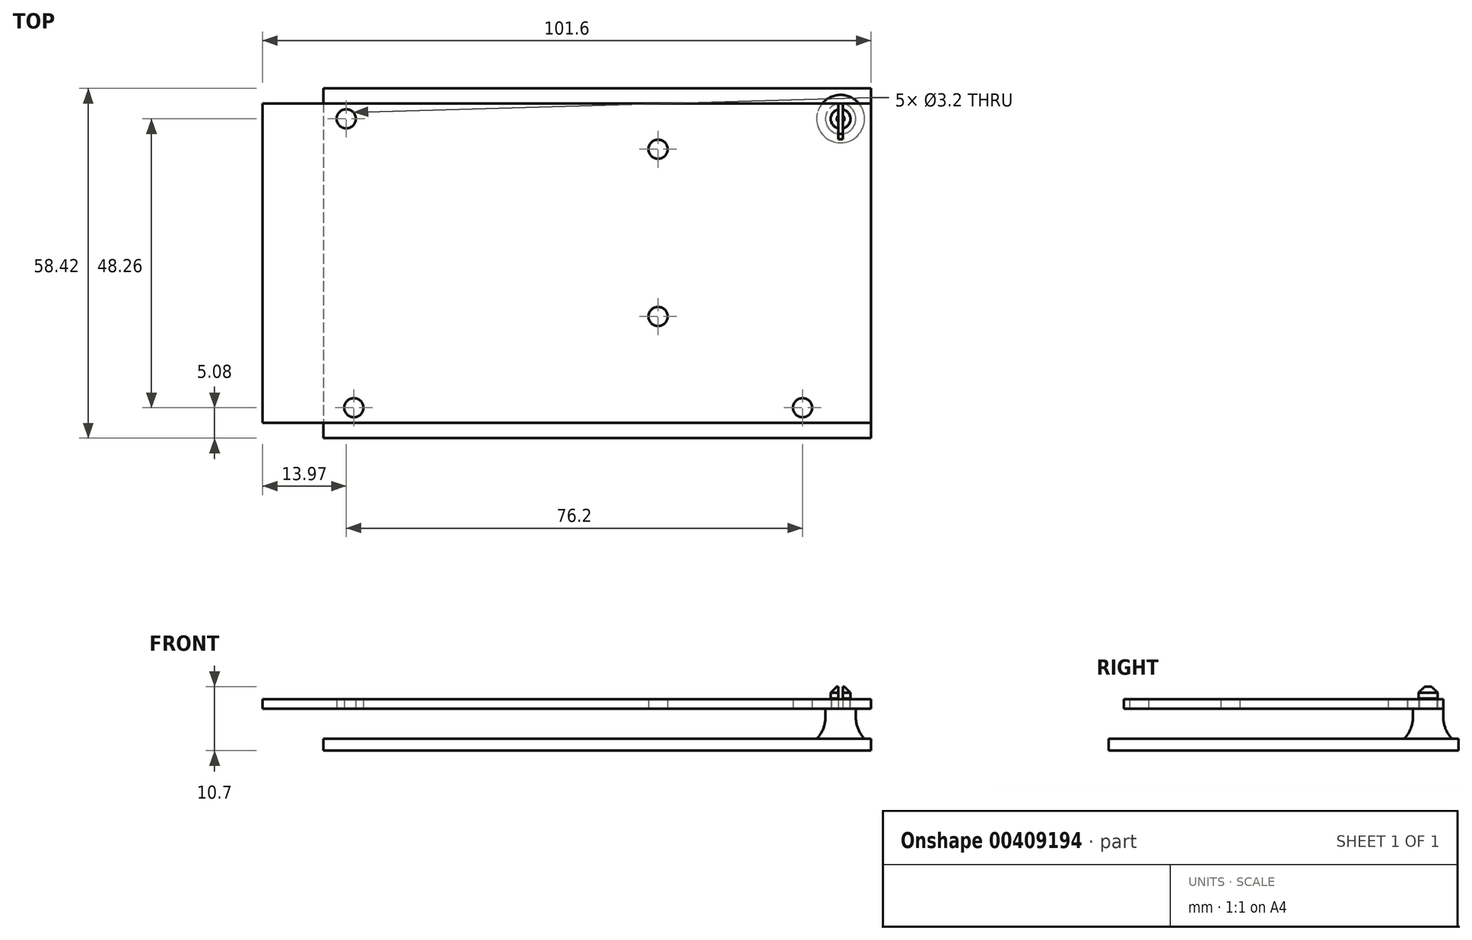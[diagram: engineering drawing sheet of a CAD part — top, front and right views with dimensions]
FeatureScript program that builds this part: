
annotation { "Feature Type Name" : "Feature", "Feature Type Description" : "" }
export const myFeature = defineFeature(function(context is Context, id is Id, definition is map)
    precondition{}
    {
        {
            var Q0;
            Q0=qCreatedBy(makeId("Top.planeOp"),FACE);
            var sketch = newSketch(context, id + "F0", { "sketchPlane" : qUnion([Q0])});
            skLineSegment(sketch, "E0.bottom", {"start": v(-50.8, -26.67) * mm, "end": v(50.8, -26.67) * mm});
            skLineSegment(sketch, "E0.top", {"start": v(-50.8, 26.67) * mm, "end": v(50.8, 26.67) * mm});
            skLineSegment(sketch, "E0.left", {"start": v(-50.8, -26.67) * mm, "end": v(-50.8, 26.67) * mm});
            skLineSegment(sketch, "E0.right", {"start": v(50.8, -26.67) * mm, "end": v(50.8, 26.67) * mm});
            skCircle(sketch, "E1", {"center": v(45.72, 24.13) * mm, "radius": 1.6 * mm});
            skCircle(sketch, "E2", {"center": v(15.24, 19.05) * mm, "radius": 1.6 * mm});
            skCircle(sketch, "E3", {"center": v(15.24, -8.9) * mm, "radius": 1.6 * mm});
            skCircle(sketch, "E4", {"center": v(39.37, -24.13) * mm, "radius": 1.6 * mm});
            skCircle(sketch, "E5", {"center": v(-35.56, -24.13) * mm, "radius": 1.6 * mm});
            skCircle(sketch, "E6", {"center": v(-36.83, 24.13) * mm, "radius": 1.6 * mm});
            skLineSegment(sketch, "E7", {"start": v(-36.83, 24.13) * mm, "end": v(45.72, 24.13) * mm, "construction": true});
            skLineSegment(sketch, "E8", {"start": v(-35.56, -24.13) * mm, "end": v(39.37, -24.13) * mm, "construction": true});
            skLineSegment(sketch, "E9", {"start": v(15.24, 19.05) * mm, "end": v(15.24, -8.9) * mm, "construction": true});
            skSolve(sketch);
        }
        {
            var Q0;
            Q0 = qSketchRegion(id + "F0", true);
            extrude(context, id + "F1", {"entities" : qUnion([Q0]), "depth" : 1.6 * mm});
        }
        {
            var Q0;
            Q0=makeQuery(id+"F1.opExtrude","CAP_FACE",FACE,{"disambiguationData":[OSD([sQuery(id+"F0.wireOp",EDGE,"E0.bottom"),sQuery(id+"F0.wireOp",EDGE,"E0.top"),sQuery(id+"F0.wireOp",EDGE,"E0.left"),sQuery(id+"F0.wireOp",EDGE,"E0.right"),sQuery(id+"F0.wireOp",EDGE,"E1"),sQuery(id+"F0.wireOp",EDGE,"E2"),sQuery(id+"F0.wireOp",EDGE,"E3"),sQuery(id+"F0.wireOp",EDGE,"E4"),sQuery(id+"F0.wireOp",EDGE,"E5"),sQuery(id+"F0.wireOp",EDGE,"E6")])],"isStart":true});
            var sketch = newSketch(context, id + "F2", { "sketchPlane" : qUnion([Q0])});
            skCircle(sketch, "E10", {"center": v(45.72, -24.13) * mm, "radius": 2.54 * mm});
            skSolve(sketch);
        }
        {
            var Q0;
            Q0 = qSketchRegion(id + "F2", true);
            extrude(context, id + "F3", {"entities" : qUnion([Q0]), "depth" : 5 * mm});
        }
        {
            var Q0;
            Q0=makeQuery(id+"F3.opExtrude","CAP_FACE",FACE,{"disambiguationData":[OSD([sQuery(id+"F2.wireOp",EDGE,"E10")])],"isStart":true});
            var sketch = newSketch(context, id + "F4", { "sketchPlane" : qUnion([Q0])});
            skCircle(sketch, "E11", {"center": v(45.72, 24.13) * mm, "radius": 1.5 * mm});
            skSolve(sketch);
        }
        {
            var Q0;
            Q0 = qSketchRegion(id + "F4", true);
            extrude(context, id + "F5", {"entities" : qUnion([Q0]), "operationType" : NewBodyOperationType.ADD, "depth" : 3.7 * mm});
        }
        {
            var Q0;
            Q0=makeQuery(id+"F5.opExtrude","CAP_FACE",FACE,{"disambiguationData":[OSD([sQuery(id+"F4.wireOp",EDGE,"E11")])],"isStart":false});
            var sketch = newSketch(context, id + "F6", { "sketchPlane" : qUnion([Q0])});
            skCircle(sketch, "E12", {"center": v(45.72, 24.13) * mm, "radius": 1.65 * mm});
            skSolve(sketch);
        }
        {
            var Q0;
            Q0=makeQuery(id+"F6.imprint","IMPRINT",FACE,{"disambiguationData":[TD([[makeQuery(id+"F6.imprint","IMPRINT",EDGE,{"derivedFrom":sQuery(id+"F6.wireOp",EDGE,"E12")}),1.0]])]});
            extrude(context, id + "F7", {"entities" : qUnion([Q0]), "operationType" : NewBodyOperationType.ADD, "oppositeDirection" : true, "depth" : (3.7 - 1.7) * mm});
        }
        {
            var Q0;
            Q0=makeQuery(id+"F7.opExtrude","CAP_EDGE",EDGE,{"disambiguationData":[OSD([sQuery(id+"F6.wireOp",EDGE,"E12")])],"isStart":true});
            chamfer(context, id + "F8", {"entities" : qUnion([Q0]), "width" : (1) * mm, "tangentPropagation" : true});
        }
        {
            var Q0;
            {var subQ0=sQuery(id+"F4.wireOp",EDGE,"E11");Q0=makeQuery(id+"F7.boolean.opBoolean","MERGE",FACE,{"derivedFrom":[makeQuery(id+"F5.opExtrude","CAP_FACE",FACE,{"disambiguationData":[OSD([subQ0])],"isStart":false}),makeQuery(id+"F7.opExtrude","CAP_FACE",FACE,{"disambiguationData":[OSD([subQ0,sQuery(id+"F6.wireOp",EDGE,"E12")])],"isStart":true})]});}
            var sketch = newSketch(context, id + "F9", { "sketchPlane" : qUnion([Q0])});
            skLineSegment(sketch, "E13.bottom", {"start": v(45.32, 27.5) * mm, "end": v(46.12, 27.5) * mm});
            skLineSegment(sketch, "E13.top", {"start": v(45.32, 20.75) * mm, "end": v(46.12, 20.75) * mm});
            skLineSegment(sketch, "E13.left", {"start": v(45.32, 27.5) * mm, "end": v(45.32, 20.75) * mm});
            skLineSegment(sketch, "E13.right", {"start": v(46.12, 27.5) * mm, "end": v(46.12, 20.75) * mm});
            skPoint(sketch, "E13.middle", {"position": v(45.72, 24.13) * mm});
            skSolve(sketch);
        }
        {
            var Q0;
            {var subQ0=sQuery(id+"F9.wireOp",EDGE,"E13.left");var subQ1=sQuery(id+"F6.wireOp",EDGE,"E12");var subQ2=sQuery(id+"F4.wireOp",EDGE,"E11");var subQ3=makeQuery(id+"F8.opChamfer","BLEND_EDGE",EDGE,{"blendedFrom":[makeQuery(id+"F7.opExtrude","CAP_EDGE",EDGE,{"disambiguationData":[OSD([subQ1])],"isStart":true}),makeQuery(id+"F7.boolean.opBoolean","MERGE",FACE,{"derivedFrom":[makeQuery(id+"F5.opExtrude","CAP_FACE",FACE,{"disambiguationData":[OSD([subQ2])],"isStart":false}),makeQuery(id+"F7.opExtrude","CAP_FACE",FACE,{"disambiguationData":[OSD([subQ2,subQ1])],"isStart":true})]})],"blendedInto":[makeQuery(id+"F7.boolean.opBoolean","MERGE",FACE,{"derivedFrom":[makeQuery(id+"F5.opExtrude","CAP_FACE",FACE,{"disambiguationData":[OSD([subQ2])],"isStart":false}),makeQuery(id+"F7.opExtrude","CAP_FACE",FACE,{"disambiguationData":[OSD([subQ2,subQ1])],"isStart":true})]})]});var subQ4=makeQuery(id+"F9.imprint","INTERSECT",VERTEX,{"disambiguationData":[OD(0.0)],"derivedFrom":[subQ3,subQ0]});Q0=makeQuery(id+"F9.imprint","IMPRINT",FACE,{"disambiguationData":[TD([[makeQuery(id+"F9.imprint","IMPRINT",EDGE,{"disambiguationData":[TD([[subQ4,-1.0]])],"derivedFrom":subQ0}),1.0]])]});}
            var Q1;
            {var subQ0=sQuery(id+"F9.wireOp",EDGE,"E13.top");Q1=makeQuery(id+"F9.imprint","IMPRINT",FACE,{"disambiguationData":[TD([[makeQuery(id+"F9.imprint","IMPRINT",EDGE,{"derivedFrom":subQ0}),1.0]])]});}
            var Q2;
            {var subQ0=sQuery(id+"F9.wireOp",EDGE,"E13.bottom");Q2=makeQuery(id+"F9.imprint","IMPRINT",FACE,{"disambiguationData":[TD([[makeQuery(id+"F9.imprint","IMPRINT",EDGE,{"derivedFrom":subQ0}),-1.0]])]});}
            extrude(context, id + "F10", {"entities" : qUnion([Q0, Q1, Q2]), "operationType" : NewBodyOperationType.REMOVE, "oppositeDirection" : true, "depth" : 3.7 * mm});
        }
        {
            var Q0;
            Q0=makeQuery(id+"F3.opExtrude","CAP_FACE",FACE,{"disambiguationData":[OSD([sQuery(id+"F2.wireOp",EDGE,"E10")])],"isStart":false});
            var sketch = newSketch(context, id + "F11", { "sketchPlane" : qUnion([Q0])});
            skLineSegment(sketch, "E14.bottom", {"start": v(50.8, -29.2) * mm, "end": v(-40.64, -29.2) * mm});
            skLineSegment(sketch, "E14.top", {"start": v(50.8, 29.21) * mm, "end": v(-40.64, 29.21) * mm});
            skLineSegment(sketch, "E14.left", {"start": v(50.8, -29.2) * mm, "end": v(50.8, 29.21) * mm});
            skLineSegment(sketch, "E14.right", {"start": v(-40.64, -29.2) * mm, "end": v(-40.64, 29.21) * mm});
            skCircle(sketch, "E15", {"center": v(45.72, -24.13) * mm, "radius": 5.08 * mm, "construction": true});
            skCircle(sketch, "E16", {"center": v(-35.56, 24.13) * mm, "radius": 5.08 * mm, "construction": true});
            skSolve(sketch);
        }
        {
            var Q0;
            Q0 = qSketchRegion(id + "F11", true);
            extrude(context, id + "F12", {"entities" : qUnion([Q0]), "depth" : 2 * mm});
        }
        {
            var Q0;
            Q0=makeQuery(id+"F3.opExtrude","CAP_FACE",FACE,{"disambiguationData":[OSD([sQuery(id+"F2.wireOp",EDGE,"E10")])],"isStart":false});
            var sketch = newSketch(context, id + "F13", { "sketchPlane" : qUnion([Q0])});
            skCircle(sketch, "E17", {"center": v(45.72, -24.13) * mm, "radius": 4 * mm});
            skSolve(sketch);
        }
        {
            var Q0;
            Q0 = qSketchRegion(id + "F13", true);
            var Q1;
            Q1=sQuery(id+"F13.wireOp",EDGE,"E17");
            extrude(context, id + "F14", {"entities" : qUnion([Q0]), "operationType" : NewBodyOperationType.ADD, "surfaceEntities" : qUnion([Q1]), "oppositeDirection" : true, "depth" : 0.01 * mm});
        }
        {
            var Q0;
            Q0=makeQuery(id+"F14.boolean.opBoolean","INTERSECT",EDGE,{"derivedFrom":[makeQuery(id+"F3.opExtrude","SWEPT_FACE",FACE,{"disambiguationData":[OSD([sQuery(id+"F2.wireOp",EDGE,"E10")])]}),makeQuery(id+"F14.opExtrude","CAP_FACE",FACE,{"disambiguationData":[OSD([sQuery(id+"F13.wireOp",EDGE,"E17")])],"isStart":false})]});
            fillet(context, id + "F15", {"entities" : qUnion([Q0]), "radius" : 5 * mm, "tangentPropagation" : true, "allowEdgeOverflow" : false});
        }
    });
